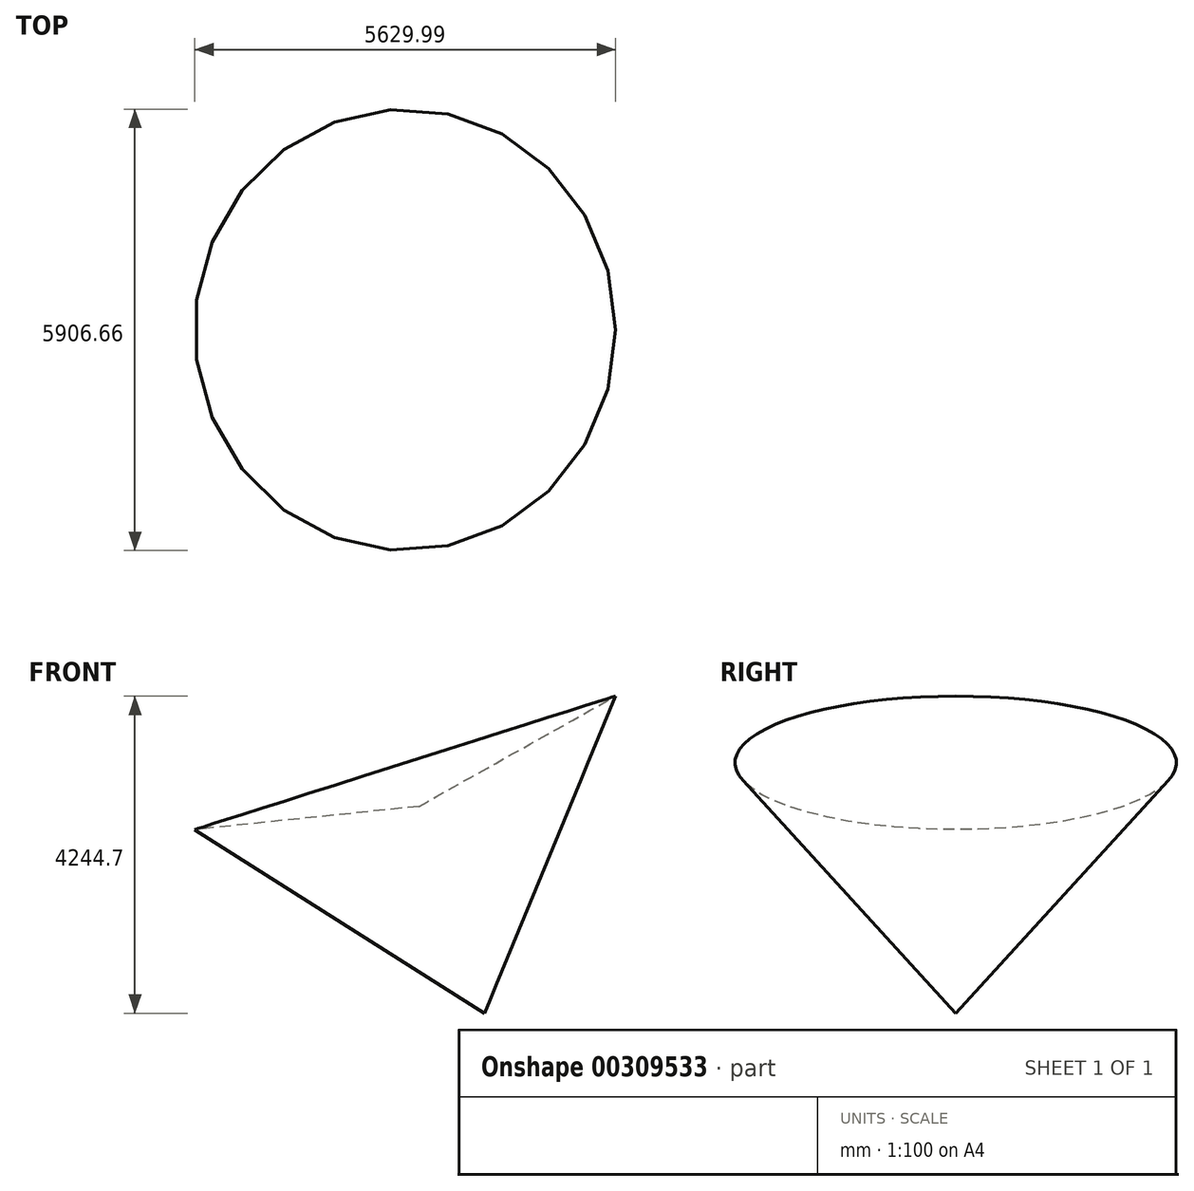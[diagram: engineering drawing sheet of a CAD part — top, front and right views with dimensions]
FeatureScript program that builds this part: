
annotation { "Feature Type Name" : "Feature", "Feature Type Description" : "" }
export const myFeature = defineFeature(function(context is Context, id is Id, definition is map)
    precondition{}
    {
        {
            var Q0;
            Q0=qCreatedBy(makeId("Front.planeOp"),FACE);
            var sketch = newSketch(context, id + "F0", { "sketchPlane" : qUnion([Q0])});
            skPoint(sketch, "E0.first.point", {"position": v(0, 0) * mm});
            skCircle(sketch, "E1", {"center": v(0, 0) * mm, "radius": 3016 * mm});
            skLineSegment(sketch, "E2", {"start": v(-3000, -310.3) * mm, "end": v(0, 0) * mm});
            skLineSegment(sketch, "E3", {"start": v(0, 0) * mm, "end": v(902.95, -2845.4) * mm});
            skLineSegment(sketch, "E4", {"start": v(-3000, -310.3) * mm, "end": v(1000, -2845.4) * mm});
            skSolve(sketch);
        }
        {
            var Q0;
            {var subQ0=sQuery(id+"F0.wireOp",EDGE,"E2");Q0=makeQuery(id+"F0.imprint","IMPRINT",FACE,{"disambiguationData":[TD([[makeQuery(id+"F0.imprint","IMPRINT",EDGE,{"derivedFrom":subQ0}),-1.0]])]});}
            var Q1;
            Q1=sQuery(id+"F0.wireOp",EDGE,"E3");
            revolve(context, id + "F1", {"entities" : qUnion([Q0]), "axis" : qUnion([Q1]), "revolveType" : RevolveType.FULL});
        }
    });
